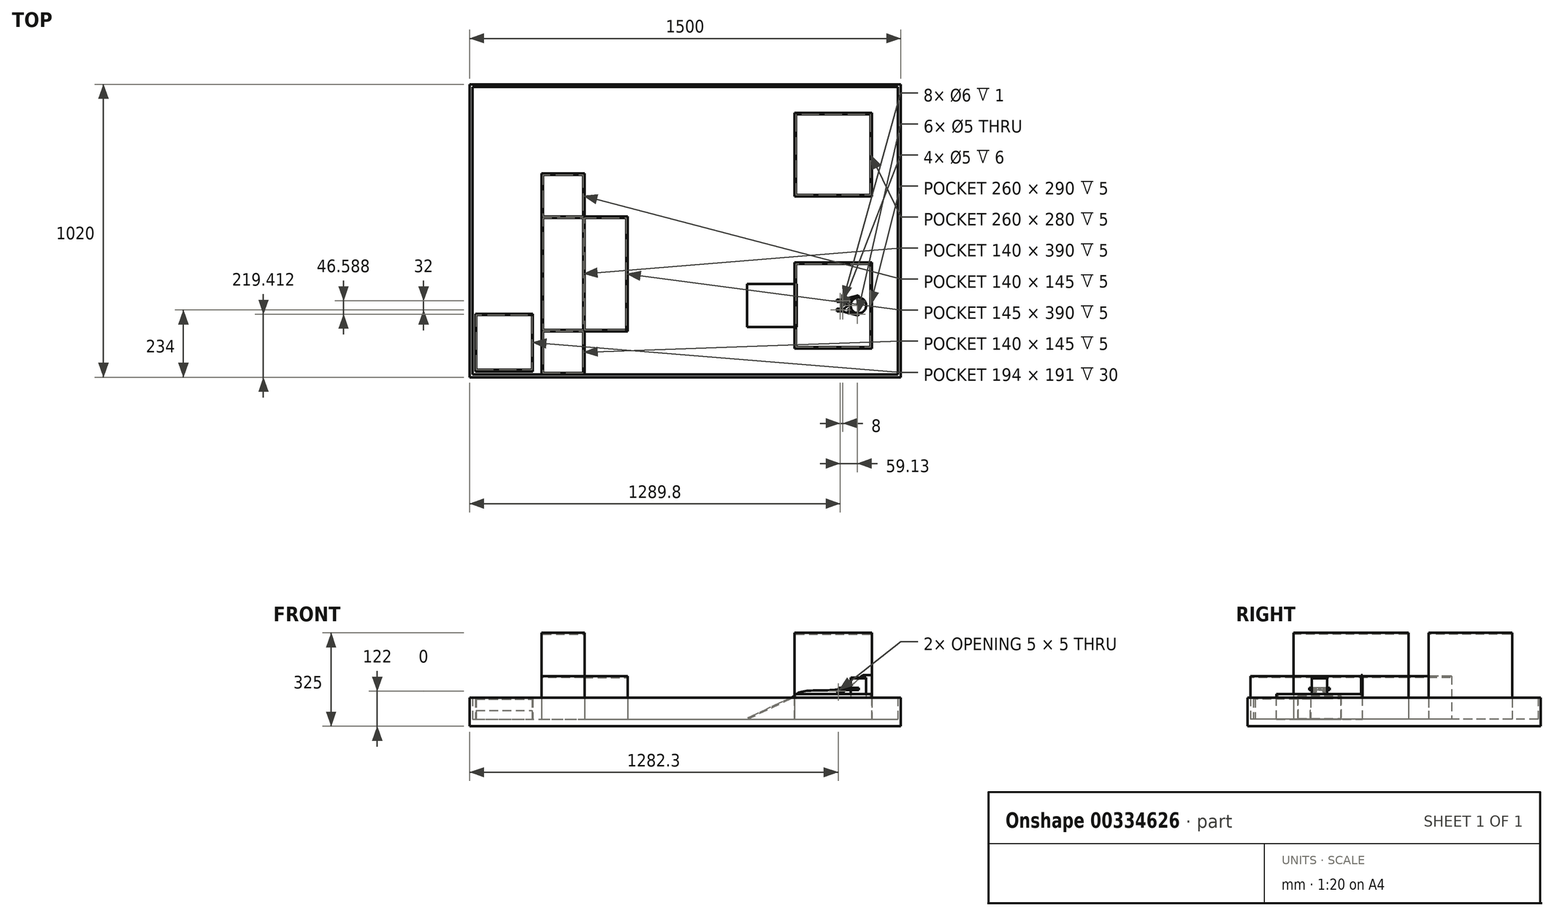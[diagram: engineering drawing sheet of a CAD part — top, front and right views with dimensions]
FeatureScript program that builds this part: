
annotation { "Feature Type Name" : "Feature", "Feature Type Description" : "" }
export const myFeature = defineFeature(function(context is Context, id is Id, definition is map)
    precondition{}
    {
        {
            var Q0;
            Q0=qCreatedBy(makeId("Top.planeOp"),FACE);
            var sketch = newSketch(context, id + "F0", { "sketchPlane" : qUnion([Q0])});
            skCircle(sketch, "E0", {"center": v(0, 0) * mm, "radius": 27.2 * mm});
            skSolve(sketch);
        }
        {
            var Q0;
            Q0=qSketchRegion(id+"F0",true);
            extrude(context, id + "F1", {"entities" : qUnion([Q0]), "depth" : 2.83 * mm});
        }
        {
            var Q0;
            Q0=makeQuery(id+"F1.opExtrude","CAP_FACE",FACE,{"disambiguationData":[OSD([sQuery(id+"F0.wireOp",EDGE,"E0")])],"isStart":false});
            var sketch = newSketch(context, id + "F2", { "sketchPlane" : qUnion([Q0])});
            skCircle(sketch, "E1", {"center": v(0, 0) * mm, "radius": 26.4 * mm});
            skSolve(sketch);
        }
        {
            var Q0;
            Q0=qSketchRegion(id+"F2",true);
            extrude(context, id + "F3", {"entities" : qUnion([Q0]), "operationType" : NewBodyOperationType.ADD, "depth" : 67.36 * mm});
        }
        {
            var Q0;
            Q0=makeQuery(id+"F3.opExtrude","CAP_FACE",FACE,{"disambiguationData":[OSD([sQuery(id+"F2.wireOp",EDGE,"E1")])],"isStart":false});
            var sketch = newSketch(context, id + "F4", { "sketchPlane" : qUnion([Q0])});
            skCircle(sketch, "E2", {"center": v(0, 0) * mm, "radius": 27.2 * mm});
            skSolve(sketch);
        }
        {
            var Q0;
            Q0=qSketchRegion(id+"F4",true);
            extrude(context, id + "F5", {"entities" : qUnion([Q0]), "operationType" : NewBodyOperationType.ADD, "depth" : 2.83 * mm});
        }
        {
            var Q0;
            Q0=makeQuery(id+"F5.opExtrude","CAP_FACE",FACE,{"disambiguationData":[OSD([sQuery(id+"F4.wireOp",EDGE,"E2")])],"isStart":false});
            var sketch = newSketch(context, id + "F6", { "sketchPlane" : qUnion([Q0])});
            skSolve(sketch);
        }
        {
            var Q0;
            Q0=qCreatedBy(makeId("Top.planeOp"),FACE);
            cPlane(context, id + "F7", {"entities" : qUnion([Q0]), "cplaneType" : CPlaneType.OFFSET, "offset" : 25 * mm, "width" : 150 * mm, "height" : 150 * mm});
        }
        {
            var Q0;
            Q0=makeQuery(id+"F6.imprint","IMPRINT",FACE,{"disambiguationData":[TD([[makeQuery(id+"F6.imprint","IMPRINT",EDGE,{"derivedFrom":makeQuery(id+"F5.opExtrude","CAP_EDGE",EDGE,{"disambiguationData":[OSD([sQuery(id+"F4.wireOp",EDGE,"E2")])],"isStart":false})}),1.0]])]});
            var sketch = newSketch(context, id + "F8", { "sketchPlane" : qUnion([Q0])});
            skSolve(sketch);
        }
        {
            var Q0;
            Q0=qCreatedBy(makeId("Top.planeOp"),FACE);
            var sketch = newSketch(context, id + "F9", { "sketchPlane" : qUnion([Q0])});
            skLineSegment(sketch, "E3.bottom", {"start": v(-222.8, -150) * mm, "end": v(47.2, -150) * mm});
            skLineSegment(sketch, "E3.top", {"start": v(-222.8, 150) * mm, "end": v(47.2, 150) * mm});
            skLineSegment(sketch, "E3.left", {"start": v(-222.8, -150) * mm, "end": v(-222.8, 150) * mm});
            skLineSegment(sketch, "E3.right", {"start": v(47.2, -150) * mm, "end": v(47.2, 150) * mm});
            skSolve(sketch);
        }
        {
            var Q0;
            Q0=qSketchRegion(id+"F9",true);
            extrude(context, id + "F10", {"entities" : qUnion([Q0]), "oppositeDirection" : true, "depth" : 72 * mm});
        }
        {
            var Q0;
            Q0=makeQuery(id+"F10.opExtrude","CAP_FACE",FACE,{"disambiguationData":[OSD([sQuery(id+"F9.wireOp",EDGE,"E3.bottom"),sQuery(id+"F9.wireOp",EDGE,"E3.top"),sQuery(id+"F9.wireOp",EDGE,"E3.left"),sQuery(id+"F9.wireOp",EDGE,"E3.right")])],"isStart":true});
            var sketch = newSketch(context, id + "F11", { "sketchPlane" : qUnion([Q0])});
            skLineSegment(sketch, "E4.bottom", {"start": v(-222.8, -150) * mm, "end": v(47.2, -150) * mm});
            skLineSegment(sketch, "E4.top", {"start": v(-222.8, -145) * mm, "end": v(42.2, -145) * mm});
            skLineSegment(sketch, "E4.left", {"start": v(-222.8, -150) * mm, "end": v(-222.8, -145) * mm});
            skLineSegment(sketch, "E5.bottom", {"start": v(47.2, 150) * mm, "end": v(42.2, 150) * mm});
            skLineSegment(sketch, "E5.left", {"start": v(47.2, 150) * mm, "end": v(47.2, -150) * mm});
            skLineSegment(sketch, "E5.right", {"start": v(42.2, 150) * mm, "end": v(42.2, -145) * mm});
            skSolve(sketch);
        }
        {
            var Q0;
            Q0=qSketchRegion(id+"F11",true);
            extrude(context, id + "F12", {"entities" : qUnion([Q0]), "operationType" : NewBodyOperationType.ADD, "depth" : 15 * mm});
        }
        {
            var Q0;
            Q0=makeQuery(id+"F12.boolean.opBoolean","MERGE",FACE,{"derivedFrom":[makeQuery(id+"F10.opExtrude","SWEPT_FACE",FACE,{"disambiguationData":[OSD([sQuery(id+"F9.wireOp",EDGE,"E3.top")])]}),makeQuery(id+"F12.opExtrude","SWEPT_FACE",FACE,{"disambiguationData":[OSD([sQuery(id+"F11.wireOp",EDGE,"E5.bottom")])]})]});
            var sketch = newSketch(context, id + "F13", { "sketchPlane" : qUnion([Q0])});
            skLineSegment(sketch, "E6", {"start": v(-47.2, 81.36) * mm, "end": v(-21.31, 81.36) * mm});
            skFitSpline(sketch, "E7", {"points": [v(-21.31, 81.36) * mm, v(15.24, 52.01) * mm, v(114.14, 28.17) * mm, v(222.8, 0) * mm], "startDerivative": vector(181.02, 0.3) * mm, "endDerivative": vector(-1.73, -239.85) * mm});
            skLineSegment(sketch, "E8", {"start": v(-47.2, 81.36) * mm, "end": v(-47.2, -72) * mm});
            skLineSegment(sketch, "E9", {"start": v(-47.2, -72) * mm, "end": v(222.8, -72) * mm});
            skLineSegment(sketch, "E10", {"start": v(222.8, -72) * mm, "end": v(222.8, 0) * mm});
            skSolve(sketch);
        }
        {
            var Q0;
            Q0=qSketchRegion(id+"F13",true);
            extrude(context, id + "F14", {"entities" : qUnion([Q0]), "operationType" : NewBodyOperationType.ADD, "oppositeDirection" : true, "depth" : 5 * mm});
        }
        {
            var Q0;
            Q0=makeQuery(id+"F10.opExtrude","CAP_FACE",FACE,{"disambiguationData":[OSD([sQuery(id+"F9.wireOp",EDGE,"E3.bottom"),sQuery(id+"F9.wireOp",EDGE,"E3.top"),sQuery(id+"F9.wireOp",EDGE,"E3.left"),sQuery(id+"F9.wireOp",EDGE,"E3.right")])],"isStart":true});
            var sketch = newSketch(context, id + "F15", { "sketchPlane" : qUnion([Q0])});
            skLineSegment(sketch, "E11.bottom", {"start": v(-222.8, 145) * mm, "end": v(-217.8, 145) * mm});
            skLineSegment(sketch, "E11.top", {"start": v(-222.8, -145) * mm, "end": v(-217.8, -145) * mm});
            skLineSegment(sketch, "E11.left", {"start": v(-222.8, 145) * mm, "end": v(-222.8, -145) * mm});
            skLineSegment(sketch, "E11.right", {"start": v(-217.8, 145) * mm, "end": v(-217.8, -145) * mm});
            skSolve(sketch);
        }
        {
            var Q0;
            Q0=qSketchRegion(id+"F15",true);
            extrude(context, id + "F16", {"entities" : qUnion([Q0]), "operationType" : NewBodyOperationType.ADD, "depth" : 5 * mm});
        }
        {
            var Q0;
            Q0=makeQuery(id+"F10.opExtrude","CAP_FACE",FACE,{"disambiguationData":[OSD([sQuery(id+"F9.wireOp",EDGE,"E3.bottom"),sQuery(id+"F9.wireOp",EDGE,"E3.top"),sQuery(id+"F9.wireOp",EDGE,"E3.left"),sQuery(id+"F9.wireOp",EDGE,"E3.right")])],"isStart":false});
            var sketch = newSketch(context, id + "F17", { "sketchPlane" : qUnion([Q0])});
            skLineSegment(sketch, "E12.bottom", {"start": v(147.2, 250) * mm, "end": v(-1352.8, 250) * mm});
            skLineSegment(sketch, "E12.top", {"start": v(147.2, -770) * mm, "end": v(-1352.8, -770) * mm});
            skLineSegment(sketch, "E12.left", {"start": v(147.2, 250) * mm, "end": v(147.2, -770) * mm});
            skLineSegment(sketch, "E12.right", {"start": v(-1352.8, 250) * mm, "end": v(-1352.8, -770) * mm});
            skSolve(sketch);
        }
        {
            var Q0;
            Q0=qSketchRegion(id+"F17",true);
            extrude(context, id + "F18", {"entities" : qUnion([Q0]), "operationType" : NewBodyOperationType.ADD, "depth" : 25 * mm});
        }
        {
            var Q0;
            Q0=makeQuery(id+"F18.opExtrude","CAP_FACE",FACE,{"disambiguationData":[OSD([sQuery(id+"F17.wireOp",EDGE,"E12.bottom"),sQuery(id+"F17.wireOp",EDGE,"E12.top"),sQuery(id+"F17.wireOp",EDGE,"E12.left"),sQuery(id+"F17.wireOp",EDGE,"E12.right")])],"isStart":true});
            var sketch = newSketch(context, id + "F19", { "sketchPlane" : qUnion([Q0])});
            skLineSegment(sketch, "E13.bottom", {"start": v(-222.8, 670) * mm, "end": v(47.2, 670) * mm});
            skLineSegment(sketch, "E13.top", {"start": v(-222.8, 380) * mm, "end": v(47.2, 380) * mm});
            skLineSegment(sketch, "E13.left", {"start": v(-222.8, 670) * mm, "end": v(-222.8, 380) * mm});
            skLineSegment(sketch, "E13.right", {"start": v(47.2, 670) * mm, "end": v(47.2, 380) * mm});
            skSolve(sketch);
        }
        {
            var Q0;
            Q0=qSketchRegion(id+"F19",true);
            extrude(context, id + "F20", {"entities" : qUnion([Q0]), "operationType" : NewBodyOperationType.ADD, "depth" : 300 * mm});
        }
        {
            var Q0;
            Q0=makeQuery(id+"F20.opExtrude","CAP_FACE",FACE,{"disambiguationData":[OSD([sQuery(id+"F19.wireOp",EDGE,"E13.bottom"),sQuery(id+"F19.wireOp",EDGE,"E13.top"),sQuery(id+"F19.wireOp",EDGE,"E13.left"),sQuery(id+"F19.wireOp",EDGE,"E13.right")])],"isStart":false});
            var sketch = newSketch(context, id + "F21", { "sketchPlane" : qUnion([Q0])});
            skLineSegment(sketch, "E14.bottom", {"start": v(-217.8, 665) * mm, "end": v(42.2, 665) * mm});
            skLineSegment(sketch, "E14.top", {"start": v(-217.8, 385) * mm, "end": v(42.2, 385) * mm});
            skLineSegment(sketch, "E14.left", {"start": v(-217.8, 665) * mm, "end": v(-217.8, 385) * mm});
            skLineSegment(sketch, "E14.right", {"start": v(42.2, 665) * mm, "end": v(42.2, 385) * mm});
            skSolve(sketch);
        }
        {
            var Q0;
            Q0=qSketchRegion(id+"F21",true);
            extrude(context, id + "F22", {"entities" : qUnion([Q0]), "operationType" : NewBodyOperationType.REMOVE, "oppositeDirection" : true, "depth" : 5 * mm});
        }
        {
            var Q0;
            Q0=makeQuery(id+"F18.opExtrude","CAP_FACE",FACE,{"disambiguationData":[OSD([sQuery(id+"F17.wireOp",EDGE,"E12.bottom"),sQuery(id+"F17.wireOp",EDGE,"E12.top"),sQuery(id+"F17.wireOp",EDGE,"E12.left"),sQuery(id+"F17.wireOp",EDGE,"E12.right")])],"isStart":true});
            var sketch = newSketch(context, id + "F23", { "sketchPlane" : qUnion([Q0])});
            skLineSegment(sketch, "E15.bottom", {"start": v(-1352.8, 770) * mm, "end": v(147.2, 770) * mm});
            skLineSegment(sketch, "E15.top", {"start": v(-1352.8, -250) * mm, "end": v(147.2, -250) * mm});
            skLineSegment(sketch, "E15.left", {"start": v(-1352.8, 770) * mm, "end": v(-1352.8, -250) * mm});
            skLineSegment(sketch, "E15.right", {"start": v(147.2, 770) * mm, "end": v(147.2, -250) * mm});
            skLineSegment(sketch, "E16.bottom", {"start": v(-1342.8, 760) * mm, "end": v(137.2, 760) * mm});
            skLineSegment(sketch, "E16.top", {"start": v(-1342.8, -240) * mm, "end": v(137.2, -240) * mm});
            skLineSegment(sketch, "E16.left", {"start": v(-1342.8, 760) * mm, "end": v(-1342.8, -240) * mm});
            skLineSegment(sketch, "E16.right", {"start": v(137.2, 760) * mm, "end": v(137.2, -240) * mm});
            skSolve(sketch);
        }
        {
            var Q0;
            Q0=qSketchRegion(id+"F23",true);
            extrude(context, id + "F24", {"entities" : qUnion([Q0]), "operationType" : NewBodyOperationType.ADD, "depth" : 75 * mm});
        }
        {
            var Q0;
            Q0=makeQuery(id+"F18.opExtrude","CAP_FACE",FACE,{"disambiguationData":[OSD([sQuery(id+"F17.wireOp",EDGE,"E12.bottom"),sQuery(id+"F17.wireOp",EDGE,"E12.top"),sQuery(id+"F17.wireOp",EDGE,"E12.left"),sQuery(id+"F17.wireOp",EDGE,"E12.right")])],"isStart":true});
            var sketch = newSketch(context, id + "F25", { "sketchPlane" : qUnion([Q0])});
            skLineSegment(sketch, "E17.bottom", {"start": v(-1102.8, 460) * mm, "end": v(-952.8, 460) * mm});
            skLineSegment(sketch, "E17.top", {"start": v(-1102.8, -240) * mm, "end": v(-952.8, -240) * mm});
            skLineSegment(sketch, "E17.left", {"start": v(-1102.8, 460) * mm, "end": v(-1102.8, -240) * mm});
            skLineSegment(sketch, "E17.right", {"start": v(-952.8, 460) * mm, "end": v(-952.8, 310) * mm});
            skLineSegment(sketch, "E18.bottom", {"start": v(-952.8, 310) * mm, "end": v(-802.8, 310) * mm});
            skLineSegment(sketch, "E18.top", {"start": v(-952.8, -90) * mm, "end": v(-802.8, -90) * mm});
            skLineSegment(sketch, "E18.right", {"start": v(-802.8, 310) * mm, "end": v(-802.8, -90) * mm});
            skLineSegment(sketch, "E19.trimOffspring", {"start": v(-952.8, -90) * mm, "end": v(-952.8, -240) * mm});
            skSolve(sketch);
        }
        {
            var Q0;
            Q0=qSketchRegion(id+"F25",true);
            extrude(context, id + "F26", {"entities" : qUnion([Q0]), "operationType" : NewBodyOperationType.ADD, "depth" : 150 * mm});
        }
        {
            var Q0;
            Q0=makeQuery(id+"F26.opExtrude","CAP_FACE",FACE,{"disambiguationData":[OSD([sQuery(id+"F25.wireOp",EDGE,"E17.bottom"),sQuery(id+"F25.wireOp",EDGE,"E17.top"),sQuery(id+"F25.wireOp",EDGE,"E17.left"),sQuery(id+"F25.wireOp",EDGE,"E17.right"),sQuery(id+"F25.wireOp",EDGE,"E18.bottom"),sQuery(id+"F25.wireOp",EDGE,"E18.top"),sQuery(id+"F25.wireOp",EDGE,"E18.right"),sQuery(id+"F25.wireOp",EDGE,"E19.trimOffspring")])],"isStart":false});
            var sketch = newSketch(context, id + "F27", { "sketchPlane" : qUnion([Q0])});
            skLineSegment(sketch, "E20.bottom", {"start": v(-952.8, 310) * mm, "end": v(-1102.8, 310) * mm});
            skLineSegment(sketch, "E20.top", {"start": v(-952.8, -90) * mm, "end": v(-1102.8, -90) * mm});
            skLineSegment(sketch, "E20.left", {"start": v(-952.8, 310) * mm, "end": v(-952.8, -90) * mm});
            skLineSegment(sketch, "E20.right", {"start": v(-1102.8, 310) * mm, "end": v(-1102.8, -90) * mm});
            skSolve(sketch);
        }
        {
            var Q0;
            Q0=qSketchRegion(id+"F27",true);
            extrude(context, id + "F28", {"entities" : qUnion([Q0]), "operationType" : NewBodyOperationType.ADD, "depth" : 150 * mm});
        }
        {
            var Q0;
            Q0=makeQuery(id+"F28.opExtrude","CAP_FACE",FACE,{"disambiguationData":[OSD([sQuery(id+"F27.wireOp",EDGE,"E20.bottom"),sQuery(id+"F27.wireOp",EDGE,"E20.top"),sQuery(id+"F27.wireOp",EDGE,"E20.left"),sQuery(id+"F27.wireOp",EDGE,"E20.right")])],"isStart":false});
            var sketch = newSketch(context, id + "F29", { "sketchPlane" : qUnion([Q0])});
            skLineSegment(sketch, "E21.bottom", {"start": v(-1097.8, 305) * mm, "end": v(-957.8, 305) * mm});
            skLineSegment(sketch, "E21.top", {"start": v(-1097.8, -85) * mm, "end": v(-957.8, -85) * mm});
            skLineSegment(sketch, "E21.left", {"start": v(-1097.8, 305) * mm, "end": v(-1097.8, -85) * mm});
            skLineSegment(sketch, "E21.right", {"start": v(-957.8, 305) * mm, "end": v(-957.8, -85) * mm});
            skSolve(sketch);
        }
        {
            var Q0;
            Q0=qSketchRegion(id+"F29",true);
            extrude(context, id + "F30", {"entities" : qUnion([Q0]), "operationType" : NewBodyOperationType.REMOVE, "oppositeDirection" : true, "depth" : 5 * mm});
        }
        {
            var Q0;
            {var subQ0=sQuery(id+"F25.wireOp",EDGE,"E17.left");var subQ1=sQuery(id+"F25.wireOp",EDGE,"E18.bottom");var subQ2=sQuery(id+"F25.wireOp",EDGE,"E17.right");var subQ3=sQuery(id+"F25.wireOp",EDGE,"E17.bottom");var subQ4=makeQuery(id+"F26.opExtrude","CAP_FACE",FACE,{"disambiguationData":[OSD([subQ3,sQuery(id+"F25.wireOp",EDGE,"E17.top"),subQ0,subQ2,subQ1,sQuery(id+"F25.wireOp",EDGE,"E18.top"),sQuery(id+"F25.wireOp",EDGE,"E18.right"),sQuery(id+"F25.wireOp",EDGE,"E19.trimOffspring")])],"isStart":false});Q0=makeQuery(id+"F28.boolean.opBoolean","SPLIT",FACE,{"disambiguationData":[TD([makeQuery(id+"F26.opExtrude","SWEPT_FACE",FACE,{"disambiguationData":[OSD([subQ3])]})])],"derivedFrom":subQ4});}
            var sketch = newSketch(context, id + "F31", { "sketchPlane" : qUnion([Q0])});
            skLineSegment(sketch, "E22.bottom", {"start": v(-1097.8, 455) * mm, "end": v(-957.8, 455) * mm});
            skLineSegment(sketch, "E22.top", {"start": v(-1097.8, 310) * mm, "end": v(-957.8, 310) * mm});
            skLineSegment(sketch, "E22.left", {"start": v(-1097.8, 455) * mm, "end": v(-1097.8, 310) * mm});
            skLineSegment(sketch, "E22.right", {"start": v(-957.8, 455) * mm, "end": v(-957.8, 310) * mm});
            skLineSegment(sketch, "E23.bottom", {"start": v(-952.8, 305) * mm, "end": v(-807.8, 305) * mm});
            skLineSegment(sketch, "E23.top", {"start": v(-952.8, -85) * mm, "end": v(-807.8, -85) * mm});
            skLineSegment(sketch, "E23.left", {"start": v(-952.8, 305) * mm, "end": v(-952.8, -85) * mm});
            skLineSegment(sketch, "E23.right", {"start": v(-807.8, 305) * mm, "end": v(-807.8, -85) * mm});
            skLineSegment(sketch, "E24.bottom", {"start": v(-1097.8, -90) * mm, "end": v(-957.8, -90) * mm});
            skLineSegment(sketch, "E24.top", {"start": v(-1097.8, -235) * mm, "end": v(-957.8, -235) * mm});
            skLineSegment(sketch, "E24.left", {"start": v(-1097.8, -90) * mm, "end": v(-1097.8, -235) * mm});
            skLineSegment(sketch, "E24.right", {"start": v(-957.8, -90) * mm, "end": v(-957.8, -235) * mm});
            skSolve(sketch);
        }
        {
            var Q0;
            Q0=qSketchRegion(id+"F31",true);
            extrude(context, id + "F32", {"entities" : qUnion([Q0]), "operationType" : NewBodyOperationType.REMOVE, "oppositeDirection" : true, "depth" : 5 * mm});
        }
        {
            var Q0;
            Q0=qCreatedBy(id+"F7.planeOp",FACE);
            var sketch = newSketch(context, id + "F33", { "sketchPlane" : qUnion([Q0])});
            skLineSegment(sketch, "E25", {"start": v(0, 0) * mm, "end": v(-90, 0) * mm, "construction": true});
            skLineSegment(sketch, "E26.bottom", {"start": v(-74.5, -12) * mm, "end": v(-55, -12) * mm});
            skLineSegment(sketch, "E26.top", {"start": v(-74.5, -20) * mm, "end": v(-55, -20) * mm});
            skLineSegment(sketch, "E26.left", {"start": v(-74.5, -12) * mm, "end": v(-74.5, -13) * mm});
            skPoint(sketch, "E27.visualSharp", {"position": v(-51, -12) * mm});
            skPoint(sketch, "E28.visualSharp", {"position": v(-51, -20) * mm});
            skCircle(sketch, "E29", {"center": v(-55, -16) * mm, "radius": 3 * mm});
            skLineSegment(sketch, "E30", {"start": v(-59, -3.98) * mm, "end": v(-59, -18.08) * mm, "construction": true});
            skCircle(sketch, "E31.MirrorC", {"center": v(-63, -16) * mm, "radius": 3 * mm});
            skLineSegment(sketch, "E32.bottom", {"start": v(-74.5, -13) * mm, "end": v(-65.65, -13) * mm});
            skLineSegment(sketch, "E32.top", {"start": v(-74.5, -19) * mm, "end": v(-65.65, -19) * mm});
            skArc(sketch, "E33", {"start": v(-65.65, -13) * mm, "mid": v(-67, -16) * mm, "end": v(-65.65, -19) * mm});
            skLineSegment(sketch, "E34.trimOffspring", {"start": v(-74.5, -19) * mm, "end": v(-74.5, -20) * mm});
            skArc(sketch, "E35.trimOffspring", {"start": v(-55, -20) * mm, "mid": v(-51, -16) * mm, "end": v(-55, -12) * mm});
            skLineSegment(sketch, "E36.MirrorCS", {"start": v(-74.5, 12) * mm, "end": v(-74.5, 13) * mm});
            skLineSegment(sketch, "E37.MirrorCS", {"start": v(-74.5, 19) * mm, "end": v(-74.5, 20) * mm});
            skPoint(sketch, "E38.MirrorP", {"position": v(-51, 12) * mm});
            skLineSegment(sketch, "E39.MirrorCS", {"start": v(-74.5, 12) * mm, "end": v(-55, 12) * mm});
            skPoint(sketch, "E40.MirrorP", {"position": v(-51, 20) * mm});
            skArc(sketch, "E41.MirrorCS", {"start": v(-65.65, 13) * mm, "mid": v(-67, 16) * mm, "end": v(-65.65, 19) * mm});
            skArc(sketch, "E42.MirrorCS", {"start": v(-55, 20) * mm, "mid": v(-51, 16) * mm, "end": v(-55, 12) * mm});
            skLineSegment(sketch, "E43.MirrorCS", {"start": v(-74.5, 20) * mm, "end": v(-55, 20) * mm});
            skCircle(sketch, "E44.MirrorC", {"center": v(-55, 16) * mm, "radius": 3 * mm});
            skCircle(sketch, "E45.MirrorC", {"center": v(-63, 16) * mm, "radius": 3 * mm});
            skLineSegment(sketch, "E46.MirrorCS", {"start": v(-74.5, 19) * mm, "end": v(-65.65, 19) * mm});
            skLineSegment(sketch, "E47.MirrorCS", {"start": v(-74.5, 13) * mm, "end": v(-65.65, 13) * mm});
            skSolve(sketch);
        }
        {
            var Q0;
            Q0=qSketchRegion(id+"F33",true);
            var Q1;
            Q1=qSketchRegion(id+"F36",true);
            extrude(context, id + "F34", {"entities" : qUnion([Q0, Q1]), "endBound" : BoundingType.SYMMETRIC, "depth" : 8 * mm});
        }
        {
            var Q0;
            Q0=makeQuery(id+"F34.opExtrude","CAP_EDGE",EDGE,{"disambiguationData":[OSD([sQuery(id+"F33.wireOp",EDGE,"E34.trimOffspring")])],"isStart":false});
            var Q1;
            Q1=makeQuery(id+"F34.opExtrude","CAP_EDGE",EDGE,{"disambiguationData":[OSD([sQuery(id+"F33.wireOp",EDGE,"E26.left")])],"isStart":false});
            var Q2;
            Q2=makeQuery(id+"F34.opExtrude","CAP_EDGE",EDGE,{"disambiguationData":[OSD([sQuery(id+"F33.wireOp",EDGE,"E34.trimOffspring")])],"isStart":true});
            var Q3;
            Q3=makeQuery(id+"F34.opExtrude","CAP_EDGE",EDGE,{"disambiguationData":[OSD([sQuery(id+"F33.wireOp",EDGE,"E26.left")])],"isStart":true});
            var Q4;
            Q4=makeQuery(id+"F34.opExtrude","CAP_EDGE",EDGE,{"disambiguationData":[OSD([sQuery(id+"F33.wireOp",EDGE,"E36.MirrorCS")])],"isStart":false});
            var Q5;
            Q5=makeQuery(id+"F34.opExtrude","CAP_EDGE",EDGE,{"disambiguationData":[OSD([sQuery(id+"F33.wireOp",EDGE,"E37.MirrorCS")])],"isStart":false});
            var Q6;
            Q6=makeQuery(id+"F34.opExtrude","CAP_EDGE",EDGE,{"disambiguationData":[OSD([sQuery(id+"F33.wireOp",EDGE,"E37.MirrorCS")])],"isStart":true});
            var Q7;
            Q7=makeQuery(id+"F34.opExtrude","CAP_EDGE",EDGE,{"disambiguationData":[OSD([sQuery(id+"F33.wireOp",EDGE,"E36.MirrorCS")])],"isStart":true});
            fillet(context, id + "F35", {"entities" : qUnion([Q0, Q1, Q2, Q3, Q4, Q5, Q6, Q7]), "radius" : 4 * mm, "tangentPropagation" : true, "allowEdgeOverflow" : false});
        }
        {
            var Q0;
            Q0=makeQuery(id+"F34.opExtrude","SWEPT_FACE",FACE,{"disambiguationData":[OSD([sQuery(id+"F33.wireOp",EDGE,"E26.top")])]});
            var sketch = newSketch(context, id + "F36", { "sketchPlane" : qUnion([Q0])});
            skCircle(sketch, "E48", {"center": v(-70.5, 25) * mm, "radius": 3 * mm});
            skSolve(sketch);
        }
        {
            var Q0;
            Q0=qSketchRegion(id+"F36",true);
            var Q1;
            Q1=makeQuery(id+"F34.opExtrude","SWEPT_FACE",FACE,{"disambiguationData":[OSD([sQuery(id+"F33.wireOp",EDGE,"E26.bottom")])]});
            extrude(context, id + "F37", {"entities" : qUnion([Q0]), "operationType" : NewBodyOperationType.ADD, "endBound" : BoundingType.UP_TO_SURFACE, "oppositeDirection" : true, "endBoundEntityFace" : qUnion([Q1]), "depth" : 25 * mm});
        }
        {
            var Q0;
            Q0=makeQuery(id+"F34.opExtrude","SWEPT_FACE",FACE,{"disambiguationData":[OSD([sQuery(id+"F33.wireOp",EDGE,"E43.MirrorCS")])]});
            var sketch = newSketch(context, id + "F38", { "sketchPlane" : qUnion([Q0])});
            skCircle(sketch, "E49", {"center": v(70.5, 25) * mm, "radius": 3 * mm});
            skSolve(sketch);
        }
        {
            var Q0;
            Q0=qSketchRegion(id+"F38",true);
            var Q1;
            Q1=makeQuery(id+"F34.opExtrude","SWEPT_FACE",FACE,{"disambiguationData":[OSD([sQuery(id+"F33.wireOp",EDGE,"E39.MirrorCS")])]});
            extrude(context, id + "F39", {"entities" : qUnion([Q0]), "operationType" : NewBodyOperationType.ADD, "endBound" : BoundingType.UP_TO_SURFACE, "oppositeDirection" : true, "endBoundEntityFace" : qUnion([Q1]), "depth" : 25 * mm});
        }
        {
            var Q0;
            Q0=qCreatedBy(id+"F7.planeOp",FACE);
            var sketch = newSketch(context, id + "F40", { "sketchPlane" : qUnion([Q0])});
            skCircle(sketch, "E50", {"center": v(-55, 16) * mm, "radius": 3 * mm});
            skCircle(sketch, "E51", {"center": v(-63, 16) * mm, "radius": 2.5 * mm});
            skCircle(sketch, "E52", {"center": v(-63, 16) * mm, "radius": 3 * mm});
            skCircle(sketch, "E53", {"center": v(-55, 16) * mm, "radius": 2.5 * mm});
            skSolve(sketch);
        }
        {
            var Q0;
            Q0=qSketchRegion(id+"F40",true);
            extrude(context, id + "F41", {"entities" : qUnion([Q0]), "operationType" : NewBodyOperationType.ADD, "endBound" : BoundingType.SYMMETRIC, "depth" : 6 * mm});
        }
        {
            var Q0;
            Q0=qCreatedBy(id+"F7.planeOp",FACE);
            var sketch = newSketch(context, id + "F42", { "sketchPlane" : qUnion([Q0])});
            skCircle(sketch, "E54", {"center": v(-63, -16) * mm, "radius": 2.5 * mm});
            skCircle(sketch, "E55", {"center": v(-63, -16) * mm, "radius": 3 * mm});
            skCircle(sketch, "E56", {"center": v(-55, -16) * mm, "radius": 2.5 * mm});
            skCircle(sketch, "E57", {"center": v(-55, -16) * mm, "radius": 3 * mm});
            skSolve(sketch);
        }
        {
            var Q0;
            Q0=qSketchRegion(id+"F42",true);
            extrude(context, id + "F43", {"entities" : qUnion([Q0]), "operationType" : NewBodyOperationType.ADD, "endBound" : BoundingType.SYMMETRIC, "depth" : 6 * mm});
        }
        {
            var Q0;
            Q0=makeQuery(id+"F34.opExtrude","SWEPT_FACE",FACE,{"disambiguationData":[OSD([sQuery(id+"F33.wireOp",EDGE,"E43.MirrorCS")])]});
            var sketch = newSketch(context, id + "F44", { "sketchPlane" : qUnion([Q0])});
            skArc(sketch, "E58", {"start": v(71.5, 27.3) * mm, "mid": v(70.5, 27.5) * mm, "end": v(69.5, 27.3) * mm});
            skLineSegment(sketch, "E59.bottom", {"start": v(68.2, 26) * mm, "end": v(69.5, 26) * mm});
            skLineSegment(sketch, "E59.top", {"start": v(68.2, 24) * mm, "end": v(69.5, 24) * mm});
            skLineSegment(sketch, "E60.left", {"start": v(71.5, 27.3) * mm, "end": v(71.5, 26) * mm});
            skLineSegment(sketch, "E60.right", {"start": v(69.5, 27.3) * mm, "end": v(69.5, 26) * mm});
            skPoint(sketch, "E61.orphan", {"position": v(69.5, 27.8) * mm});
            skPoint(sketch, "E62.orphan", {"position": v(71.5, 27.8) * mm});
            skArc(sketch, "E63.trimOffspring", {"start": v(68.2, 26) * mm, "mid": v(68, 25) * mm, "end": v(68.2, 24) * mm});
            skPoint(sketch, "E59.left.start.orphan", {"position": v(67.32, 26) * mm});
            skPoint(sketch, "E64.orphan", {"position": v(67.32, 24) * mm});
            skArc(sketch, "E65.trimOffspring", {"start": v(69.5, 22.7) * mm, "mid": v(70.5, 22.5) * mm, "end": v(71.5, 22.7) * mm});
            skLineSegment(sketch, "E66.trimOffspring", {"start": v(69.5, 24) * mm, "end": v(69.5, 22.7) * mm});
            skLineSegment(sketch, "E67.trimOffspring", {"start": v(71.5, 26) * mm, "end": v(72.8, 26) * mm});
            skLineSegment(sketch, "E68.trimOffspring", {"start": v(71.5, 24) * mm, "end": v(71.5, 22.7) * mm});
            skLineSegment(sketch, "E69.trimOffspring", {"start": v(71.5, 24) * mm, "end": v(72.8, 24) * mm});
            skPoint(sketch, "E60.top.end.orphan", {"position": v(69.5, 22.2) * mm});
            skPoint(sketch, "E70.orphan", {"position": v(71.5, 22.2) * mm});
            skPoint(sketch, "E59.right.end.orphan", {"position": v(73.68, 24) * mm});
            skPoint(sketch, "E71.orphan", {"position": v(73.68, 26) * mm});
            skArc(sketch, "E72.trimOffspring", {"start": v(72.8, 24) * mm, "mid": v(73, 25) * mm, "end": v(72.8, 26) * mm});
            skSolve(sketch);
        }
        {
            var Q0;
            Q0=qSketchRegion(id+"F44",true);
            extrude(context, id + "F45", {"entities" : qUnion([Q0]), "operationType" : NewBodyOperationType.REMOVE, "endBound" : BoundingType.THROUGH_ALL, "oppositeDirection" : true, "depth" : 25 * mm});
        }
        {
            var Q0;
            Q0=makeQuery(id+"F18.opExtrude","CAP_FACE",FACE,{"disambiguationData":[OSD([sQuery(id+"F17.wireOp",EDGE,"E12.bottom"),sQuery(id+"F17.wireOp",EDGE,"E12.top"),sQuery(id+"F17.wireOp",EDGE,"E12.left"),sQuery(id+"F17.wireOp",EDGE,"E12.right")])],"isStart":true});
            var sketch = newSketch(context, id + "F46", { "sketchPlane" : qUnion([Q0])});
            skLineSegment(sketch, "E73.bottom", {"start": v(-1332.8, -30) * mm, "end": v(-1132.8, -30) * mm});
            skLineSegment(sketch, "E73.top", {"start": v(-1332.8, -230) * mm, "end": v(-1132.8, -230) * mm});
            skLineSegment(sketch, "E73.left", {"start": v(-1332.8, -30) * mm, "end": v(-1332.8, -230) * mm});
            skLineSegment(sketch, "E73.right", {"start": v(-1132.8, -30) * mm, "end": v(-1132.8, -230) * mm});
            skLineSegment(sketch, "E74.bottom", {"start": v(-1329.8, -33) * mm, "end": v(-1135.8, -33) * mm});
            skLineSegment(sketch, "E74.top", {"start": v(-1329.8, -224) * mm, "end": v(-1135.8, -224) * mm});
            skLineSegment(sketch, "E74.left", {"start": v(-1329.8, -33) * mm, "end": v(-1329.8, -224) * mm});
            skLineSegment(sketch, "E74.right", {"start": v(-1135.8, -33) * mm, "end": v(-1135.8, -224) * mm});
            skSolve(sketch);
        }
        {
            var Q0;
            Q0=qSketchRegion(id+"F46",true);
            extrude(context, id + "F47", {"entities" : qUnion([Q0]), "operationType" : NewBodyOperationType.ADD, "depth" : 30 * mm});
        }
        {
            var Q0;
            Q0=makeQuery(id+"F47.opExtrude","CAP_FACE",FACE,{"disambiguationData":[OSD([sQuery(id+"F46.wireOp",EDGE,"E73.bottom"),sQuery(id+"F46.wireOp",EDGE,"E73.top"),sQuery(id+"F46.wireOp",EDGE,"E73.left"),sQuery(id+"F46.wireOp",EDGE,"E73.right"),sQuery(id+"F46.wireOp",EDGE,"E74.bottom"),sQuery(id+"F46.wireOp",EDGE,"E74.top"),sQuery(id+"F46.wireOp",EDGE,"E74.left"),sQuery(id+"F46.wireOp",EDGE,"E74.right")])],"isStart":false});
            var sketch = newSketch(context, id + "F48", { "sketchPlane" : qUnion([Q0])});
            skLineSegment(sketch, "E75.bottom", {"start": v(-1332.8, -30) * mm, "end": v(-1329.8, -30) * mm});
            skLineSegment(sketch, "E75.top", {"start": v(-1332.8, -230) * mm, "end": v(-1329.8, -230) * mm});
            skLineSegment(sketch, "E75.left", {"start": v(-1332.8, -30) * mm, "end": v(-1332.8, -230) * mm});
            skLineSegment(sketch, "E75.right", {"start": v(-1329.8, -30) * mm, "end": v(-1329.8, -224) * mm});
            skLineSegment(sketch, "E76.bottom", {"start": v(-1329.8, -230) * mm, "end": v(-1135.8, -230) * mm});
            skLineSegment(sketch, "E76.top", {"start": v(-1329.8, -224) * mm, "end": v(-1135.8, -224) * mm});
            skLineSegment(sketch, "E77.bottom", {"start": v(-1135.8, -230) * mm, "end": v(-1132.8, -230) * mm});
            skLineSegment(sketch, "E77.top", {"start": v(-1135.8, -30) * mm, "end": v(-1132.8, -30) * mm});
            skLineSegment(sketch, "E77.left", {"start": v(-1135.8, -224) * mm, "end": v(-1135.8, -30) * mm});
            skLineSegment(sketch, "E77.right", {"start": v(-1132.8, -230) * mm, "end": v(-1132.8, -30) * mm});
            skSolve(sketch);
        }
        {
            var Q0;
            Q0=qSketchRegion(id+"F48",true);
            extrude(context, id + "F49", {"entities" : qUnion([Q0]), "operationType" : NewBodyOperationType.ADD, "depth" : 40 * mm});
        }
        {
            var Q0;
            Q0=makeQuery(id+"F34.opExtrude","CAP_FACE",FACE,{"disambiguationData":[OSD([sQuery(id+"F33.wireOp",EDGE,"E36.MirrorCS"),sQuery(id+"F33.wireOp",EDGE,"E37.MirrorCS"),sQuery(id+"F33.wireOp",EDGE,"E39.MirrorCS"),sQuery(id+"F33.wireOp",EDGE,"E41.MirrorCS"),sQuery(id+"F33.wireOp",EDGE,"E42.MirrorCS"),sQuery(id+"F33.wireOp",EDGE,"E43.MirrorCS"),sQuery(id+"F33.wireOp",EDGE,"E44.MirrorC"),sQuery(id+"F33.wireOp",EDGE,"E45.MirrorC"),sQuery(id+"F33.wireOp",EDGE,"E46.MirrorCS"),sQuery(id+"F33.wireOp",EDGE,"E47.MirrorCS")])],"isStart":false});
            var sketch = newSketch(context, id + "F50", { "sketchPlane" : qUnion([Q0])});
            skLineSegment(sketch, "E78", {"start": v(-68.44, 20) * mm, "end": v(-57.46, 20) * mm});
            skLineSegment(sketch, "E79", {"start": v(-49.87, 12) * mm, "end": v(-36.83, 0) * mm});
            skLineSegment(sketch, "E80", {"start": v(-68.44, 12) * mm, "end": v(-49.87, 12) * mm});
            skLineSegment(sketch, "E81", {"start": v(-26.87, 4.21) * mm, "end": v(-38.2, 17.92) * mm});
            skLineSegment(sketch, "E82", {"start": v(-38.2, 17.92) * mm, "end": v(1.47, 28.55) * mm});
            skLineSegment(sketch, "E83", {"start": v(1.47, 28.55) * mm, "end": v(-0.63, 35.24) * mm});
            skLineSegment(sketch, "E84", {"start": v(-0.63, 35.24) * mm, "end": v(-57.46, 20) * mm});
            skCircle(sketch, "E85", {"center": v(-3.87, 30.59) * mm, "radius": 2.6 * mm});
            skCircle(sketch, "E86", {"center": v(-3.87, -30.59) * mm, "radius": 2.5 * mm});
            skCircle(sketch, "E87", {"center": v(-31.9, 0) * mm, "radius": 2.5 * mm});
            skLineSegment(sketch, "E88", {"start": v(-90.21, 0) * mm, "end": v(34.25, 0) * mm, "construction": true});
            skLineSegment(sketch, "E89", {"start": v(-36.83, 0) * mm, "end": v(-49.87, -12) * mm});
            skCircle(sketch, "E90", {"center": v(-63, -16) * mm, "radius": 2.5 * mm});
            skCircle(sketch, "E91", {"center": v(-55, -16) * mm, "radius": 2.5 * mm});
            skCircle(sketch, "E92", {"center": v(-55, 16) * mm, "radius": 2.5 * mm});
            skLineSegment(sketch, "E93", {"start": v(-68.44, 20) * mm, "end": v(-68.44, 12) * mm});
            skPoint(sketch, "E94.orphan", {"position": v(-65.65, 12) * mm});
            skLineSegment(sketch, "E95.MirrorCS", {"start": v(-68.44, -12) * mm, "end": v(-49.87, -12) * mm});
            skLineSegment(sketch, "E96.MirrorCS", {"start": v(-68.44, -20) * mm, "end": v(-68.44, -12) * mm});
            skLineSegment(sketch, "E97.MirrorCS", {"start": v(-68.44, -20) * mm, "end": v(-57.46, -20) * mm});
            skLineSegment(sketch, "E98.MirrorCS", {"start": v(-0.63, -35.24) * mm, "end": v(-57.46, -20) * mm});
            skLineSegment(sketch, "E99.MirrorCS", {"start": v(-38.2, -17.92) * mm, "end": v(1.47, -28.55) * mm});
            skLineSegment(sketch, "E100.MirrorCS", {"start": v(-26.87, -4.21) * mm, "end": v(-38.2, -17.92) * mm});
            skLineSegment(sketch, "E101.MirrorCS", {"start": v(1.47, -28.55) * mm, "end": v(-0.63, -35.24) * mm});
            skArc(sketch, "E102", {"start": v(-26.87, 4.21) * mm, "mid": v(-27.2, 0) * mm, "end": v(-26.87, -4.21) * mm});
            skPoint(sketch, "E103.orphan", {"position": v(-23.39, 0) * mm});
            skCircle(sketch, "E104.MirrorC", {"center": v(-63, 16) * mm, "radius": 2.5 * mm});
            skSolve(sketch);
        }
        {
            var Q0;
            Q0=qCreatedBy(makeId("Front.planeOp"),FACE);
            var sketch = newSketch(context, id + "F51", { "sketchPlane" : qUnion([Q0])});
            skLineSegment(sketch, "E105", {"start": v(-385.5, -72) * mm, "end": v(-222.8, 5) * mm});
            skLineSegment(sketch, "E106", {"start": v(-222.8, 5) * mm, "end": v(-214.14, 0) * mm});
            skLineSegment(sketch, "E107", {"start": v(-214.14, 0) * mm, "end": v(-214.14, 3.32) * mm});
            skLineSegment(sketch, "E108", {"start": v(-214.14, 3.32) * mm, "end": v(-222.8, 8.32) * mm});
            skLineSegment(sketch, "E109", {"start": v(-222.8, 8.32) * mm, "end": v(-386.78, -69.29) * mm});
            skLineSegment(sketch, "E110", {"start": v(-386.78, -69.29) * mm, "end": v(-385.5, -72) * mm});
            skLineSegment(sketch, "E111", {"start": v(-222.8, 8.32) * mm, "end": v(-222.8, 5) * mm});
            skSolve(sketch);
        }
        {
            var Q0;
            Q0 = qSketchRegion(id + "F51", true);
            extrude(context, id + "F52", {"entities" : qUnion([Q0]), "endBound" : BoundingType.SYMMETRIC, "depth" : 150 * mm});
        }
        {
            var Q0;
            Q0 = qSketchRegion(id + "F50", true);
            var Q1;
            Q1=makeQuery(id+"F46.imprint","IMPRINT",FACE,{"disambiguationData":[TD([[makeQuery(id+"F46.imprint","IMPRINT",EDGE,{"derivedFrom":makeQuery(id+"F10.opExtrude","CAP_EDGE",EDGE,{"disambiguationData":[OSD([sQuery(id+"F9.wireOp",EDGE,"E3.bottom")])],"isStart":false})}),1.0]])]});
            extrude(context, id + "F53", {"entities" : qUnion([Q0, Q1]), "depth" : 7.25 * mm});
        }
    });
